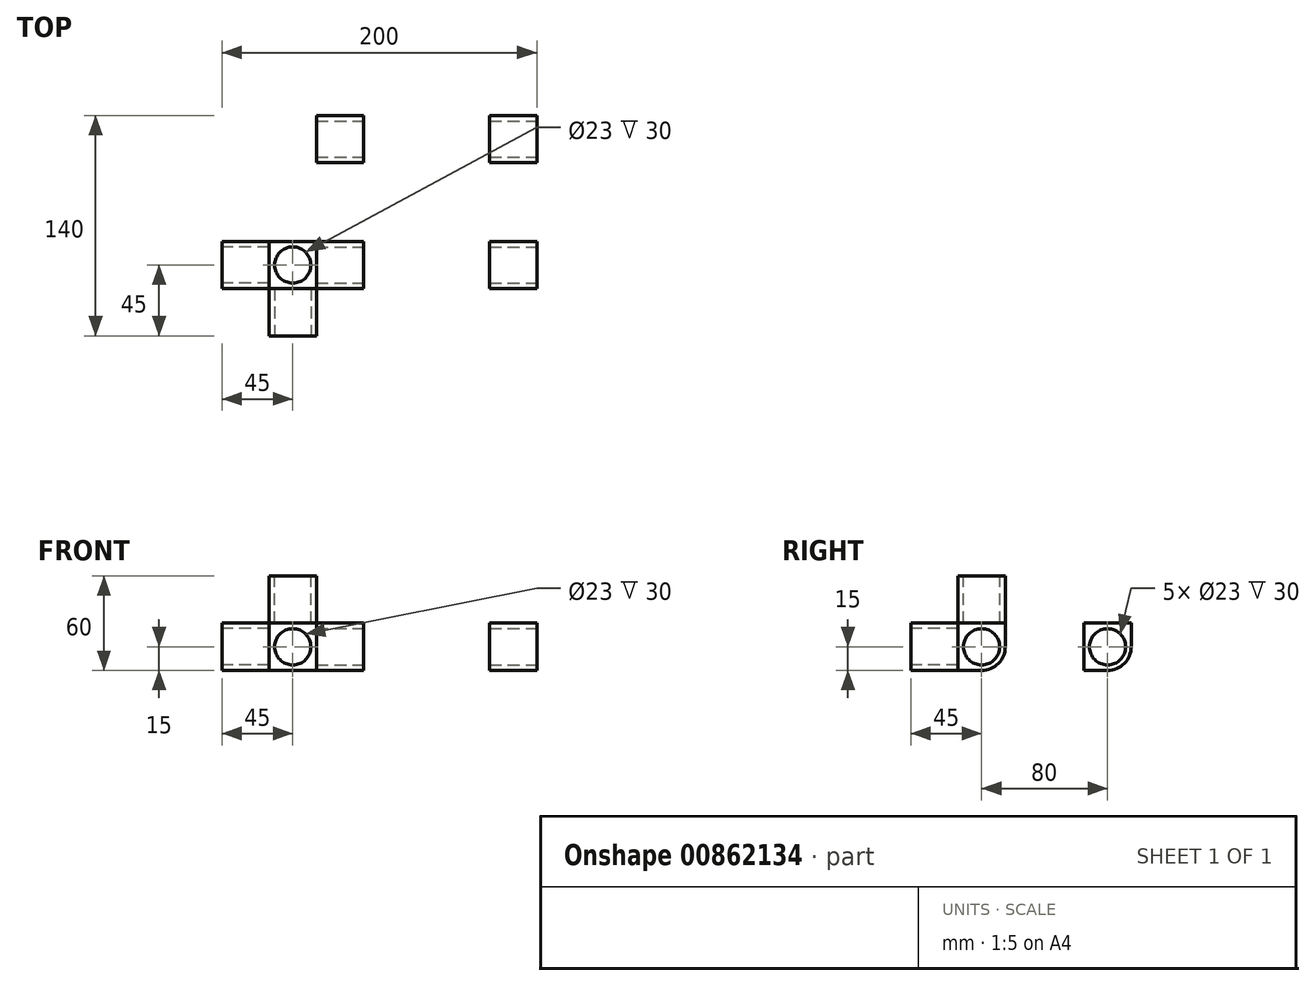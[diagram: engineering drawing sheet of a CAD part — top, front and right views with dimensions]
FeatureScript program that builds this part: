
annotation { "Feature Type Name" : "Feature", "Feature Type Description" : "" }
export const myFeature = defineFeature(function(context is Context, id is Id, definition is map)
    precondition{}
    {
        {
            var Q0;
            Q0=qCreatedBy(makeId("Top.planeOp"),FACE);
            var sketch = newSketch(context, id + "F0", { "sketchPlane" : qUnion([Q0])});
            skLineSegment(sketch, "E0.bottom", {"start": v(45, -15) * mm, "end": v(-45, -15) * mm});
            skLineSegment(sketch, "E0.top", {"start": v(45, 15) * mm, "end": v(-45, 15) * mm});
            skLineSegment(sketch, "E0.left", {"start": v(45, -15) * mm, "end": v(45, 15) * mm});
            skLineSegment(sketch, "E0.right", {"start": v(-45, -15) * mm, "end": v(-45, 15) * mm});
            skPoint(sketch, "E0.middle", {"position": v(0, 0) * mm});
            skLineSegment(sketch, "E1", {"start": v(-15, -15) * mm, "end": v(-15, -45) * mm});
            skLineSegment(sketch, "E2", {"start": v(-15, -45) * mm, "end": v(0, -45) * mm});
            skLineSegment(sketch, "E3.MirrorCS", {"start": v(15, -15) * mm, "end": v(15, -45) * mm});
            skLineSegment(sketch, "E4.MirrorCS", {"start": v(15, -45) * mm, "end": v(0, -45) * mm});
            skLineSegment(sketch, "E5", {"start": v(-15, -15) * mm, "end": v(-15, 15) * mm});
            skLineSegment(sketch, "E6", {"start": v(15, -15) * mm, "end": v(15, 15) * mm});
            skSolve(sketch);
        }
        {
            var Q0;
            {var subQ0=sQuery(id+"F0.wireOp",EDGE,"E0.right");Q0=makeQuery(id+"F0.imprint","IMPRINT",FACE,{"disambiguationData":[TD([[makeQuery(id+"F0.imprint","IMPRINT",EDGE,{"derivedFrom":subQ0}),-1.0]])]});}
            var Q1;
            {var subQ1=sQuery(id+"F0.wireOp",EDGE,"E1");Q1=makeQuery(id+"F0.imprint","IMPRINT",FACE,{"disambiguationData":[TD([[makeQuery(id+"F0.imprint","IMPRINT",EDGE,{"derivedFrom":subQ1}),1.0]])]});}
            var Q2;
            {var subQ0=sQuery(id+"F0.wireOp",EDGE,"E0.left");Q2=makeQuery(id+"F0.imprint","IMPRINT",FACE,{"disambiguationData":[TD([[makeQuery(id+"F0.imprint","IMPRINT",EDGE,{"derivedFrom":subQ0}),1.0]])]});}
            extrude(context, id + "F1", {"entities" : qUnion([Q0, Q1, Q2]), "depth" : 30 * mm, "offsetDistance" : 25 * mm});
        }
        {
            var Q0;
            {var subQ0=sQuery(id+"F0.wireOp",EDGE,"E5");Q0=makeQuery(id+"F0.imprint","IMPRINT",FACE,{"disambiguationData":[TD([[makeQuery(id+"F0.imprint","IMPRINT",EDGE,{"derivedFrom":subQ0}),-1.0]])]});}
            extrude(context, id + "F2", {"entities" : qUnion([Q0]), "depth" : 60 * mm, "offsetDistance" : 25 * mm});
        }
        {
            var Q0;
            Q0=makeQuery(id+"F2.opExtrude","CAP_FACE",FACE,{"disambiguationData":[OSD([sQuery(id+"F0.wireOp",EDGE,"E0.bottom"),sQuery(id+"F0.wireOp",EDGE,"E0.top"),sQuery(id+"F0.wireOp",EDGE,"E5"),sQuery(id+"F0.wireOp",EDGE,"E6")])],"isStart":false});
            var sketch = newSketch(context, id + "F3", { "sketchPlane" : qUnion([Q0])});
            skCircle(sketch, "E7", {"center": v(0, 0) * mm, "radius": 11.5 * mm});
            skSolve(sketch);
        }
        {
            var Q0;
            Q0=makeQuery(id+"F1.opExtrude","SWEPT_FACE",FACE,{"disambiguationData":[OSD([sQuery(id+"F0.wireOp",EDGE,"E2"),sQuery(id+"F0.wireOp",EDGE,"E4.MirrorCS")])]});
            var sketch = newSketch(context, id + "F4", { "sketchPlane" : qUnion([Q0])});
            skCircle(sketch, "E8", {"center": v(0, 15) * mm, "radius": 11.5 * mm});
            skPoint(sketch, "E8.centerSnap0", {"position": v(-15, 15) * mm});
            skPoint(sketch, "E8.centerSnap1", {"position": v(0, 0) * mm});
            skSolve(sketch);
        }
        {
            var Q0;
            Q0=makeQuery(id+"F1.opExtrude","SWEPT_FACE",FACE,{"disambiguationData":[OSD([sQuery(id+"F0.wireOp",EDGE,"E0.right")])]});
            var sketch = newSketch(context, id + "F5", { "sketchPlane" : qUnion([Q0])});
            skCircle(sketch, "E9", {"center": v(0, 15) * mm, "radius": 11.5 * mm});
            skPoint(sketch, "E9.centerSnap0", {"position": v(15, 15) * mm});
            skPoint(sketch, "E9.centerSnap1", {"position": v(0, 30) * mm});
            skSolve(sketch);
        }
        {
            var Q0;
            Q0=makeQuery(id+"F1.opExtrude","SWEPT_FACE",FACE,{"disambiguationData":[OSD([sQuery(id+"F0.wireOp",EDGE,"E0.left")])]});
            var sketch = newSketch(context, id + "F6", { "sketchPlane" : qUnion([Q0])});
            skCircle(sketch, "E10", {"center": v(0, 15) * mm, "radius": 11.5 * mm});
            skPoint(sketch, "E10.centerSnap0", {"position": v(-15, 15) * mm});
            skSolve(sketch);
        }
        {
            var Q0;
            Q0=makeQuery(id+"F3.imprint","IMPRINT",FACE,{"disambiguationData":[TD([[makeQuery(id+"F3.imprint","IMPRINT",EDGE,{"derivedFrom":sQuery(id+"F3.wireOp",EDGE,"E7")}),1.0]])]});
            extrude(context, id + "F7", {"entities" : qUnion([Q0]), "operationType" : NewBodyOperationType.REMOVE, "oppositeDirection" : true, "depth" : 30 * mm, "offsetDistance" : 25 * mm});
        }
        {
            var Q0;
            Q0=makeQuery(id+"F5.imprint","IMPRINT",FACE,{"disambiguationData":[TD([[makeQuery(id+"F5.imprint","IMPRINT",EDGE,{"derivedFrom":sQuery(id+"F5.wireOp",EDGE,"E9")}),1.0]])]});
            extrude(context, id + "F8", {"entities" : qUnion([Q0]), "operationType" : NewBodyOperationType.REMOVE, "oppositeDirection" : true, "depth" : 30 * mm, "offsetDistance" : 25 * mm});
        }
        {
            var Q0;
            Q0=makeQuery(id+"F4.imprint","IMPRINT",FACE,{"disambiguationData":[TD([[makeQuery(id+"F4.imprint","IMPRINT",EDGE,{"derivedFrom":sQuery(id+"F4.wireOp",EDGE,"E8")}),1.0]])]});
            extrude(context, id + "F9", {"entities" : qUnion([Q0]), "operationType" : NewBodyOperationType.REMOVE, "oppositeDirection" : true, "depth" : 30 * mm, "offsetDistance" : 25 * mm});
        }
        {
            var Q0;
            Q0=makeQuery(id+"F6.imprint","IMPRINT",FACE,{"disambiguationData":[TD([[makeQuery(id+"F6.imprint","IMPRINT",EDGE,{"derivedFrom":sQuery(id+"F6.wireOp",EDGE,"E10")}),1.0]])]});
            extrude(context, id + "F10", {"entities" : qUnion([Q0]), "operationType" : NewBodyOperationType.REMOVE, "oppositeDirection" : true, "depth" : 30 * mm, "offsetDistance" : 25 * mm});
        }
        {
            var Q0;
            {var subQ0=sQuery(id+"F0.wireOp",EDGE,"E0.top");Q0=makeQuery(id+"F1.opExtrude","CAP_EDGE",EDGE,{"disambiguationData":[OSD([subQ0]),TDD([makeQuery(id+"F0.imprint","IMPRINT",EDGE,{"disambiguationData":[TD([[makeQuery(id+"F0.imprint","INTERSECT",VERTEX,{"derivedFrom":[subQ0,sQuery(id+"F0.wireOp",EDGE,"E0.right")]}),1.0]])],"derivedFrom":subQ0})])],"isStart":true});}
            var Q1;
            Q1=makeQuery(id+"F2.opExtrude","CAP_EDGE",EDGE,{"disambiguationData":[OSD([sQuery(id+"F0.wireOp",EDGE,"E0.top")])],"isStart":true});
            var Q2;
            {var subQ0=sQuery(id+"F0.wireOp",EDGE,"E0.top");Q2=makeQuery(id+"F1.opExtrude","CAP_EDGE",EDGE,{"disambiguationData":[OSD([subQ0]),TDD([makeQuery(id+"F0.imprint","IMPRINT",EDGE,{"disambiguationData":[TD([[makeQuery(id+"F0.imprint","INTERSECT",VERTEX,{"derivedFrom":[subQ0,sQuery(id+"F0.wireOp",EDGE,"E0.left")]}),-1.0]])],"derivedFrom":subQ0})])],"isStart":true});}
            fillet(context, id + "F11", {"entities" : qUnion([Q0, Q1, Q2]), "radius" : 15 * mm, "tangentPropagation" : true, "allowEdgeOverflow" : false});
        }
        {
            var Q0;
            Q0=makeQuery(id+"F1.opExtrude","SWEPT_BODY",BODY,{"disambiguationData":[OSD([sQuery(id+"F0.wireOp",EDGE,"E0.bottom"),sQuery(id+"F0.wireOp",EDGE,"E0.top"),sQuery(id+"F0.wireOp",EDGE,"E0.left"),sQuery(id+"F0.wireOp",EDGE,"E6")])]});
            transform(context, id + "F12", {"entities" : qUnion([Q0]), "transformType" : TransformType.TRANSLATION_3D, "dx" : 110 * mm, "dy" : 0 * mm, "dz" : 0 * mm, "makeCopy" : true});
        }
        {
            var Q0;
            Q0=makeQuery(id+"F1.opExtrude","SWEPT_BODY",BODY,{"disambiguationData":[OSD([sQuery(id+"F0.wireOp",EDGE,"E0.bottom"),sQuery(id+"F0.wireOp",EDGE,"E0.top"),sQuery(id+"F0.wireOp",EDGE,"E0.left"),sQuery(id+"F0.wireOp",EDGE,"E6")])]});
            transform(context, id + "F13", {"entities" : qUnion([Q0]), "transformType" : TransformType.TRANSLATION_3D, "dx" : 0 * mm, "dy" : 80 * mm, "dz" : 0 * mm, "makeCopy" : true});
        }
        {
            var Q0;
            Q0=makeQuery(id+"F1.opExtrude","SWEPT_BODY",BODY,{"disambiguationData":[OSD([sQuery(id+"F0.wireOp",EDGE,"E0.bottom"),sQuery(id+"F0.wireOp",EDGE,"E0.top"),sQuery(id+"F0.wireOp",EDGE,"E0.left"),sQuery(id+"F0.wireOp",EDGE,"E6")])]});
            transform(context, id + "F14", {"entities" : qUnion([Q0]), "transformType" : TransformType.TRANSLATION_3D, "dx" : 110 * mm, "dy" : 80 * mm, "dz" : 0 * mm, "makeCopy" : true});
        }
    });
